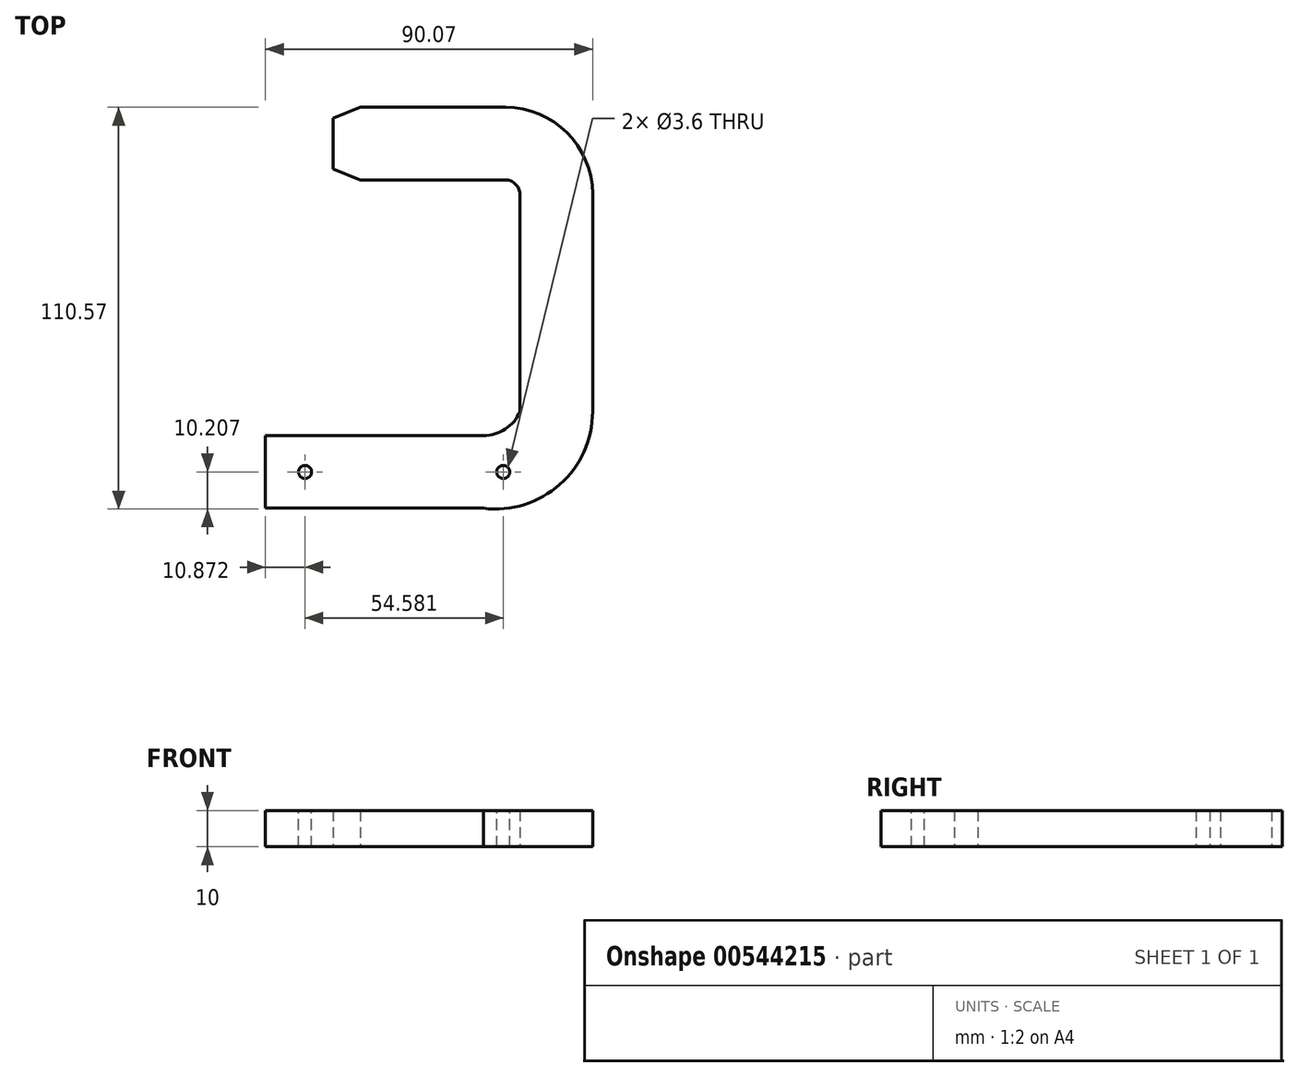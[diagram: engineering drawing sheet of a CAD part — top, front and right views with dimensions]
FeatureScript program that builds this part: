
annotation { "Feature Type Name" : "Feature", "Feature Type Description" : "" }
export const myFeature = defineFeature(function(context is Context, id is Id, definition is map)
    precondition{}
    {
        {
            var Q0;
            Q0=qCreatedBy(makeId("Top.planeOp"),FACE);
            var sketch = newSketch(context, id + "F0", { "sketchPlane" : qUnion([Q0])});
            skLineSegment(sketch, "E0.bottom", {"start": v(-168.21, 13.09) * mm, "end": v(-108.21, 13.09) * mm});
            skLineSegment(sketch, "E0.top", {"start": v(-168.21, -6.91) * mm, "end": v(-108.21, -6.91) * mm});
            skLineSegment(sketch, "E0.right", {"start": v(-108.21, 13.09) * mm, "end": v(-108.21, -6.91) * mm});
            skLineSegment(sketch, "E1", {"start": v(-104.92, 19.66) * mm, "end": v(-98.14, 19.66) * mm});
            skLineSegment(sketch, "E2", {"start": v(-98.14, 79.66) * mm, "end": v(-98.14, 19.66) * mm});
            skLineSegment(sketch, "E3.bottom", {"start": v(-98.14, 79.66) * mm, "end": v(-78.14, 79.66) * mm});
            skLineSegment(sketch, "E3.top", {"start": v(-98.14, 19.66) * mm, "end": v(-78.14, 19.66) * mm});
            skLineSegment(sketch, "E3.right", {"start": v(-78.14, 79.66) * mm, "end": v(-78.14, 19.66) * mm});
            skArc(sketch, "E4", {"start": v(-108.21, -6.91) * mm, "mid": v(-87.19, -0.4) * mm, "end": v(-78.14, 19.66) * mm});
            skArc(sketch, "E5", {"start": v(-108.21, 13.09) * mm, "mid": v(-102.2, 14.88) * mm, "end": v(-98.14, 19.66) * mm});
            skLineSegment(sketch, "E6.bottom", {"start": v(-142.14, 83.45) * mm, "end": v(-102.14, 83.45) * mm});
            skLineSegment(sketch, "E6.top", {"start": v(-142.14, 103.45) * mm, "end": v(-102.14, 103.45) * mm});
            skLineSegment(sketch, "E6.left", {"start": v(-142.14, 83.45) * mm, "end": v(-142.14, 103.45) * mm});
            skLineSegment(sketch, "E6.right", {"start": v(-102.14, 83.45) * mm, "end": v(-102.14, 103.45) * mm});
            skArc(sketch, "E7", {"start": v(-78.14, 79.66) * mm, "mid": v(-85.25, 96.5) * mm, "end": v(-102.14, 103.45) * mm});
            skArc(sketch, "E8", {"start": v(-98.14, 79.66) * mm, "mid": v(-99.39, 82.36) * mm, "end": v(-102.14, 83.45) * mm});
            skLineSegment(sketch, "E9", {"start": v(-142.14, 103.45) * mm, "end": v(-149.56, 100.45) * mm});
            skLineSegment(sketch, "E10", {"start": v(-149.56, 100.45) * mm, "end": v(-149.56, 86.45) * mm});
            skLineSegment(sketch, "E11", {"start": v(-149.56, 86.45) * mm, "end": v(-142.14, 83.45) * mm});
            skPoint(sketch, "E12.start.orphan", {"position": v(-197.45, 83.45) * mm});
            skLineSegment(sketch, "E13", {"start": v(-168.21, 13.09) * mm, "end": v(-168.21, -6.91) * mm});
            skSolve(sketch);
        }
        {
            var Q0;
            Q0 = qSketchRegion(id + "F0", true);
            extrude(context, id + "F1", {"entities" : qUnion([Q0]), "endBound" : BoundingType.SYMMETRIC, "depth" : 10 * mm, "offsetDistance" : 25 * mm});
        }
        {
            var Q0;
            Q0=makeQuery(id+"F1.opExtrude","CAP_FACE",FACE,{"disambiguationData":[OSD([sQuery(id+"F0.wireOp",EDGE,"E0.bottom"),sQuery(id+"F0.wireOp",EDGE,"E0.top"),sQuery(id+"F0.wireOp",EDGE,"E2"),sQuery(id+"F0.wireOp",EDGE,"E3.right"),sQuery(id+"F0.wireOp",EDGE,"E4"),sQuery(id+"F0.wireOp",EDGE,"E5"),sQuery(id+"F0.wireOp",EDGE,"E6.bottom"),sQuery(id+"F0.wireOp",EDGE,"E6.top"),sQuery(id+"F0.wireOp",EDGE,"E7"),sQuery(id+"F0.wireOp",EDGE,"E8"),sQuery(id+"F0.wireOp",EDGE,"E9"),sQuery(id+"F0.wireOp",EDGE,"E10"),sQuery(id+"F0.wireOp",EDGE,"E11"),sQuery(id+"F0.wireOp",EDGE,"E13")])],"isStart":false});
            var sketch = newSketch(context, id + "F2", { "sketchPlane" : qUnion([Q0])});
            skCircle(sketch, "E14", {"center": v(-157.34, 3.09) * mm, "radius": 1.8 * mm});
            skPoint(sketch, "E14.centerSnap0", {"position": v(-168.21, 3.09) * mm});
            skSolve(sketch);
        }
        {
            var Q0;
            Q0 = qSketchRegion(id + "F2", true);
            extrude(context, id + "F3", {"entities" : qUnion([Q0]), "operationType" : NewBodyOperationType.REMOVE, "oppositeDirection" : true, "depth" : 26 * mm, "offsetDistance" : 25 * mm});
        }
        {
            var Q0;
            Q0=makeQuery(id+"F1.opExtrude","CAP_FACE",FACE,{"disambiguationData":[OSD([sQuery(id+"F0.wireOp",EDGE,"E0.bottom"),sQuery(id+"F0.wireOp",EDGE,"E0.top"),sQuery(id+"F0.wireOp",EDGE,"E2"),sQuery(id+"F0.wireOp",EDGE,"E3.right"),sQuery(id+"F0.wireOp",EDGE,"E4"),sQuery(id+"F0.wireOp",EDGE,"E5"),sQuery(id+"F0.wireOp",EDGE,"E6.bottom"),sQuery(id+"F0.wireOp",EDGE,"E6.top"),sQuery(id+"F0.wireOp",EDGE,"E7"),sQuery(id+"F0.wireOp",EDGE,"E8"),sQuery(id+"F0.wireOp",EDGE,"E9"),sQuery(id+"F0.wireOp",EDGE,"E10"),sQuery(id+"F0.wireOp",EDGE,"E11"),sQuery(id+"F0.wireOp",EDGE,"E13")])],"isStart":false});
            var sketch = newSketch(context, id + "F4", { "sketchPlane" : qUnion([Q0])});
            skCircle(sketch, "E15", {"center": v(-102.76, 3.09) * mm, "radius": 1.8 * mm});
            skPoint(sketch, "E15.centerSnap0", {"position": v(-168.21, 3.09) * mm});
            skSolve(sketch);
        }
        {
            var Q0;
            Q0 = qSketchRegion(id + "F4", true);
            extrude(context, id + "F5", {"entities" : qUnion([Q0]), "operationType" : NewBodyOperationType.REMOVE, "oppositeDirection" : true, "depth" : 20 * mm, "offsetDistance" : 25 * mm});
        }
    });
